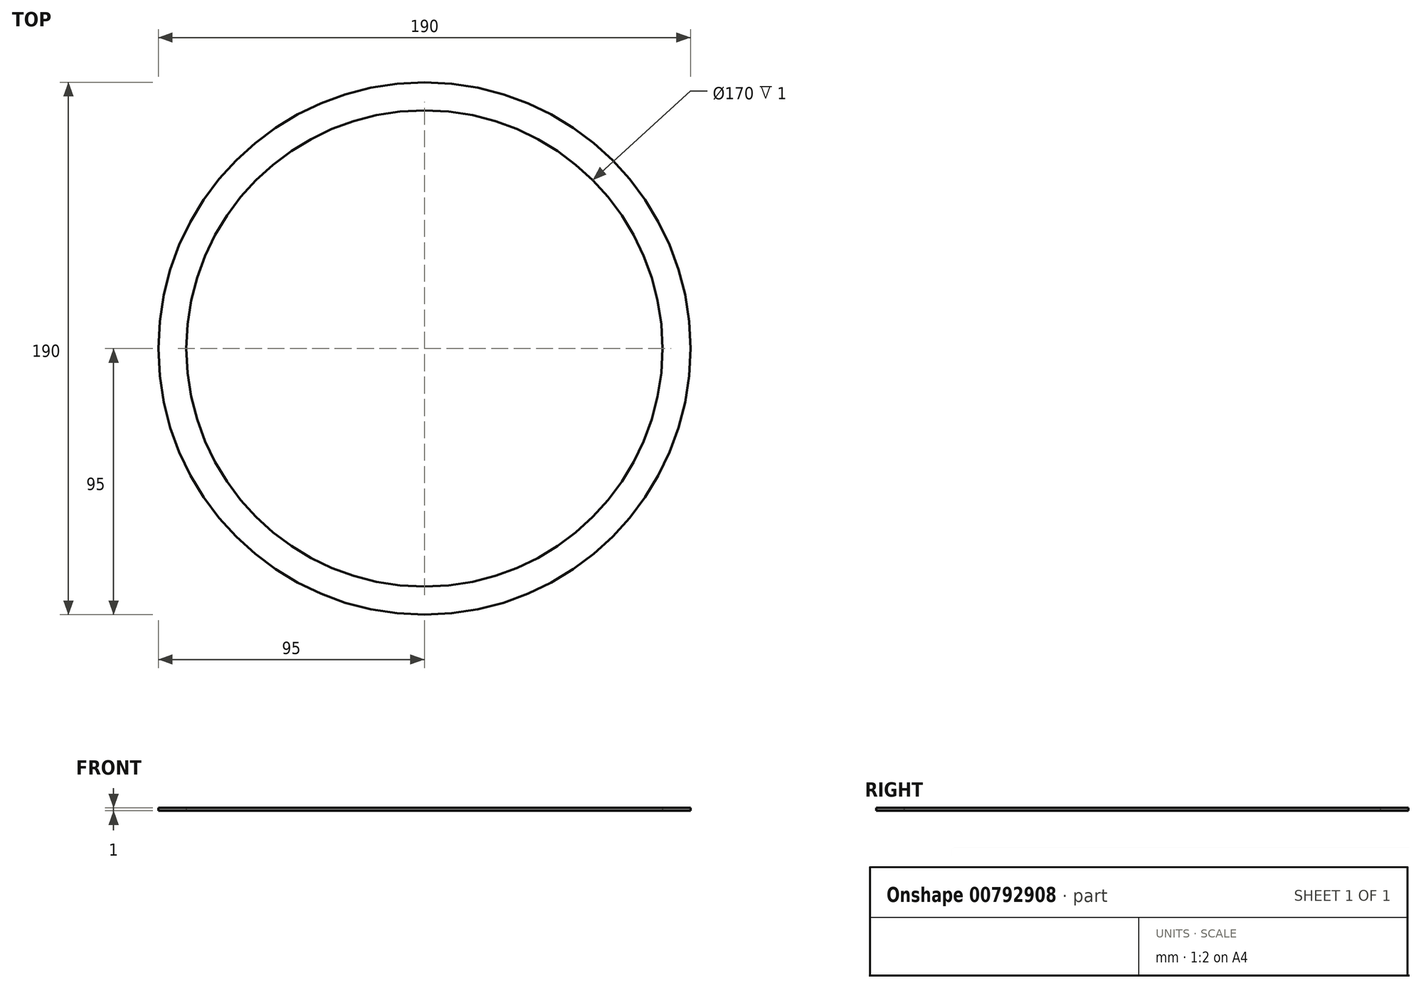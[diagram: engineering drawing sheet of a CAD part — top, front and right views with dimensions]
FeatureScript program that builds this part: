
annotation { "Feature Type Name" : "Feature", "Feature Type Description" : "" }
export const myFeature = defineFeature(function(context is Context, id is Id, definition is map)
    precondition{}
    {
        {
            var Q0;
            Q0=qCreatedBy(makeId("Top.planeOp"),FACE);
            var sketch = newSketch(context, id + "F0", { "sketchPlane" : qUnion([Q0])});
            skCircle(sketch, "E0", {"center": v(0, 0) * mm, "radius": 95 * mm});
            skCircle(sketch, "E1", {"center": v(0, 0) * mm, "radius": 85 * mm});
            skSolve(sketch);
        }
        {
            var Q0;
            Q0 = qSketchRegion(id + "F0", true);
            extrude(context, id + "F1", {"entities" : qUnion([Q0]), "depth" : 1 * mm, "offsetDistance" : 25 * mm});
        }
    });
